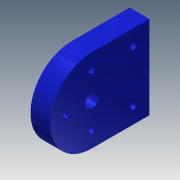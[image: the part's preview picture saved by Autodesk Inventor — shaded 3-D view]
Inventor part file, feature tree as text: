
AUTODESK INVENTOR PART (.ipt)
format: ipt  version: 2013 (Build 170138000, 138)  size: 121,344 bytes
history: native  units: mm
features: extrude x3, sketch x3
ambient origin geometry x8: Origin, YZ Plane, XZ Plane, XY Plane, X Axis, Y Axis, Z Axis, Center Point
bodies: Solid1 (feature_tree)
feature tree (6):
  extrude  "Extrusion1"  Depth=4.0mm TaperAngle=0.0deg
  extrude  "Extrusion2"  [1 undecoded]
  extrude  "Extrusion3"  [1 undecoded]
  sketch  "Sketch1"  dims[d0=17.0mm d1=0.0mm d2=4.0mm d3=0.0mm]
  sketch  "Sketch2"  dims[d4=3.0mm d5=0.0mm]
  sketch  "Sketch3"
note: 2 required parameter values undecoded (feature->parameter linkage not recoverable at this tier; creation-order binding heuristic only, values carry confidence <= 0.55)
